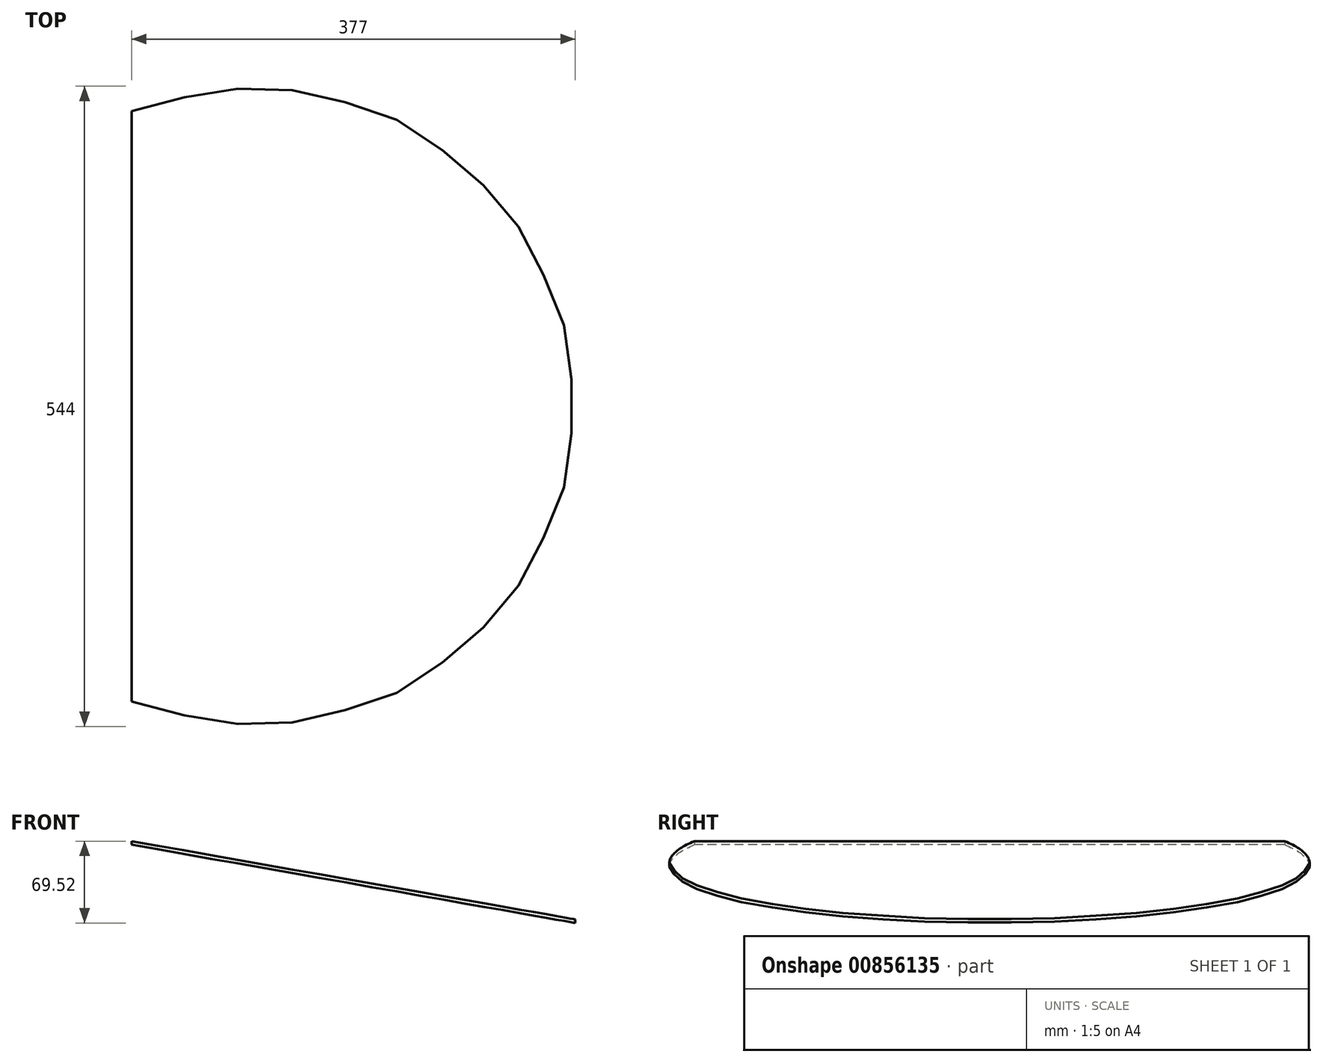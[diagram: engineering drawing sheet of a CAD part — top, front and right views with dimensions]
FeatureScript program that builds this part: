
annotation { "Feature Type Name" : "Feature", "Feature Type Description" : "" }
export const myFeature = defineFeature(function(context is Context, id is Id, definition is map)
    precondition{}
    {
        {
            var Q0;
            Q0=qCreatedBy(makeId("Top.planeOp"),FACE);
            var sketch = newSketch(context, id + "F0", { "sketchPlane" : qUnion([Q0])});
            skLineSegment(sketch, "E0", {"start": v(0, 1500.93) * mm, "end": v(0, -1708.7) * mm, "construction": true});
            skArc(sketch, "E1", {"start": v(-105, -250.92) * mm, "mid": v(272, 0) * mm, "end": v(-105, 250.92) * mm});
            skLineSegment(sketch, "E2.0", {"start": v(-105, 250.92) * mm, "end": v(-105, -250.92) * mm});
            skSolve(sketch);
        }
        {
            var Q0;
            Q0=qCreatedBy(makeId("Top.planeOp"),FACE);
            var Q1;
            Q1=sQuery(id+"F0.wireOp",EDGE,"E0");
            cPlane(context, id + "F1", {"entities" : qUnion([Q0, Q1]), "cplaneType" : CPlaneType.LINE_ANGLE, "offset" : 10 * mm, "angle" : 10 * degree, "oppositeDirection" : true, "width" : 150 * mm, "height" : 150 * mm});
        }
        {
            var Q0;
            Q0=qCreatedBy(id+"F1.planeOp",FACE);
            var sketch = newSketch(context, id + "F2", { "sketchPlane" : qUnion([Q0])});
            skCircle(sketch, "E3", {"center": v(0, 0) * mm, "radius": 300 * mm});
            skSolve(sketch);
        }
        {
            var Q0;
            Q0=makeQuery(id+"F2.imprint","IMPRINT",FACE,{"disambiguationData":[TD([[makeQuery(id+"F2.imprint","IMPRINT",EDGE,{"derivedFrom":sQuery(id+"F2.wireOp",EDGE,"E3")}),1.0]])]});
            extrude(context, id + "F3", {"entities" : qUnion([Q0]), "endBound" : BoundingType.SYMMETRIC, "depth" : 3 * mm, "offsetDistance" : 25 * mm});
        }
        {
            var Q0;
            Q0=makeQuery(id+"F0.imprint","IMPRINT",FACE,{"disambiguationData":[TD([[makeQuery(id+"F0.imprint","IMPRINT",EDGE,{"derivedFrom":sQuery(id+"F0.wireOp",EDGE,"E1")}),1.0]])]});
            extrude(context, id + "F4", {"entities" : qUnion([Q0]), "operationType" : NewBodyOperationType.INTERSECT, "endBound" : BoundingType.SYMMETRIC, "depth" : 150 * mm, "offsetDistance" : 25 * mm});
        }
    });
